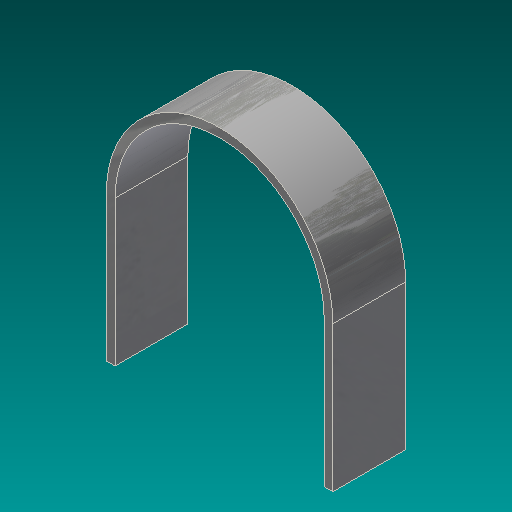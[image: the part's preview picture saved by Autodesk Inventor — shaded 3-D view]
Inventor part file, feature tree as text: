
AUTODESK INVENTOR PART (.ipt)
format: ipt  version: 2017 (Build 210142000, 142)  size: 157,696 bytes
history: native  units: in
note: dims shown in document units (in); Inventor stores cm internally (conversion verified against a paired STEP export)
features: extrude x1, sketch x1, other x1
ambient origin geometry x8: Origin, YZ Plane, XZ Plane, XY Plane, X Axis, Y Axis, Z Axis, Center Point
bodies: Solid1 (feature_tree)
feature tree (3):
  extrude  "Extrusion1"  Depth=0.12in
  sketch  "Sketch1"  dims[d0=2.875in d1=0.12in d2=2.0in d3=1.0in d4=0.0in]
  other  "Definition1"
